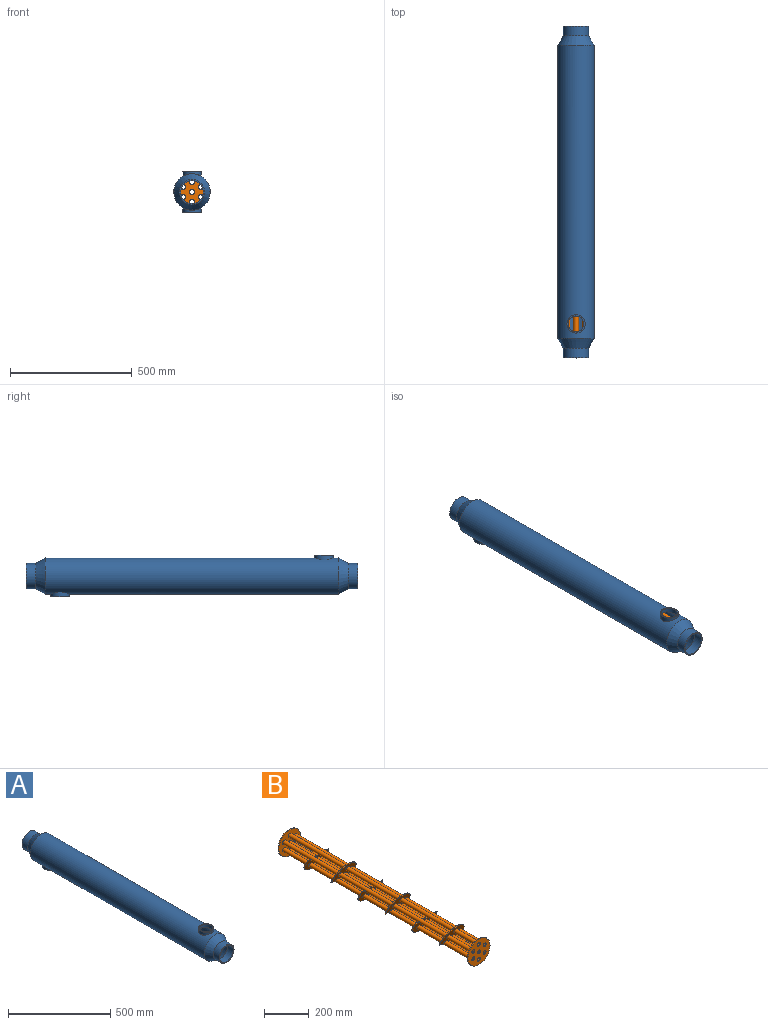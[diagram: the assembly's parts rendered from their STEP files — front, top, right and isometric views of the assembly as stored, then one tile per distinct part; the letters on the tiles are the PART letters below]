
ASSEMBLY  parts=2 mates=2
PART A: 18 faces, bbox 150x1365x170 mm
  f0: cylinder r=75mm len=1205mm, axis (0,-1,0), area 558717mm2, adj f2,f3,f14,f17
  f1: cylinder r=70mm len=1205mm, axis (0,-1,0), area 523166.6mm2, adj f7,f8,f12,f15
  f2: cone r=51.8mm half-angle=30.1deg, axis (0,-1,0), area 18420.3mm2, adj f0,f11
  f3: cone r=51.8mm half-angle=30.1deg, axis (0,1,0), area 18420.3mm2, adj f0,f4
  f4: cylinder r=51.8mm len=103.6mm, axis (0,-1,0), area 13018.8mm2, adj f3,f5
  f5: plane 103.6x103.6mm, normal (0,-1,0), area 1548.8mm2, adj f4,f6
  f6: cylinder r=46.8mm len=93.6mm, axis (0,-1,0), area 11762.2mm2, adj f5,f7
  f7: cone r=70mm half-angle=30.1deg, axis (0,1,0), area 16967.6mm2, adj f1,f6
  f8: cone r=70mm half-angle=30.1deg, axis (0,-1,0), area 16967.6mm2, adj f1,f9
  f9: cylinder r=46.8mm len=93.6mm, axis (0,-1,0), area 11762.2mm2, adj f8,f10
  f10: plane 103.6x103.6mm, normal (0,1,0), area 1548.8mm2, adj f9,f11
  f11: cylinder r=51.8mm len=103.6mm, axis (0,-1,0), area 13018.8mm2, adj f2,f10
  f12: cylinder r=32.5mm len=65mm, axis (0,0,1), area 3866.5mm2, adj f1,f16
  f13: plane 75x75mm, normal (0,0,-1), area 1099.6mm2, adj f14,f15
  f14: cylinder r=37.5mm len=75mm, axis (0,0,-1), area 3518.8mm2, adj f0,f13
  f15: cylinder r=32.5mm len=65mm, axis (0,0,-1), area 3867.9mm2, adj f1,f13
  f16: plane 75x75mm, normal (0,0,1), area 1099.6mm2, adj f12,f17
  f17: cylinder r=37.5mm len=75mm, axis (0,0,1), area 3518.1mm2, adj f0,f16
PART B: 80 faces, bbox 142.1x1207.1x142.1 mm
  f0: plane 140x140mm, normal (0,1,0), area 13409.1mm2, adj f1,f3,f4,f5,f6,f7,f8,f9
  f1: cylinder r=70mm len=140mm, axis (0,1,0), area 2199.1mm2, adj f0,f2
  f2: plane 140x140mm, normal (0,-1,0), area 12969.3mm2, adj f1,f10,f12,f13,f14,f15,f16,f18
  f3: cylinder r=9.5mm len=1205mm, axis (0,-1,0), area 71926.8mm2, adj f0,f11
  f4: cylinder r=9.5mm len=1205mm, axis (0,-1,0), area 71926.8mm2, adj f0,f11
  f5: cylinder r=9.5mm len=1205mm, axis (0,-1,0), area 71926.8mm2, adj f0,f11
  f6: cylinder r=9.5mm len=1205mm, axis (0,-1,0), area 71926.8mm2, adj f0,f11
  f7: cylinder r=9.5mm len=1205mm, axis (0,-1,0), area 71926.8mm2, adj f0,f11
  f8: cylinder r=9.5mm len=1205mm, axis (0,-1,0), area 71926.8mm2, adj f0,f11
  f9: cylinder r=9.5mm len=1205mm, axis (0,-1,0), area 71926.8mm2, adj f0,f11
  f10: cylinder r=10.5mm len=352.06mm, axis (0,-1,0), area 22715.9mm2, adj f2,f50,f55,f56,f58,f59
  f11: plane 140x140mm, normal (0,-1,0), area 13409.1mm2, adj f3,f4,f5,f6,f7,f8,f9,f61
  f12: cylinder r=10.5mm len=161.51mm, axis (0,-1,0), area 10332.2mm2, adj f2,f56
  f13: cylinder r=10.5mm len=151.95mm, axis (0,-1,0), area 9701.6mm2, adj f2,f56
  f14: cylinder r=10.5mm len=161.51mm, axis (0,-1,0), area 10332.2mm2, adj f2,f56
  f15: cylinder r=10.5mm len=352.06mm, axis (0,-1,0), area 22715.9mm2, adj f2,f50,f54,f55,f56,f58
  f16: cylinder r=10.5mm len=361.62mm, axis (0,-1,0), area 23534.1mm2, adj f2,f50
  f17: cylinder r=10.5mm len=171.06mm, axis (0,-1,0), area 10962.3mm2, adj f28,f60
  f18: cylinder r=10.5mm len=171.07mm, axis (0,-1,0), area 10962.9mm2, adj f2,f56
  f19: cylinder r=10.5mm len=175.78mm, axis (0,-1,0), area 10945.9mm2, adj f50,f58
  f20: cylinder r=10.5mm len=175.78mm, axis (0,-1,0), area 10945.9mm2, adj f44,f52
  f21: cylinder r=10.5mm len=175.78mm, axis (0,-1,0), area 10945.9mm2, adj f38,f46
  f22: cylinder r=10.5mm len=175.78mm, axis (0,-1,0), area 10945.9mm2, adj f32,f40
  f23: cylinder r=10.5mm len=175.78mm, axis (0,-1,0), area 10945.9mm2, adj f26,f34
  f24: plane 50.04x5.52mm, normal (0,0,-1), area 276.1mm2, adj f26,f28,f70,f76
  f25: plane 20.78x5.52mm, normal (0,0,-1), area 114.6mm2, adj f26,f27,f28,f76
  f26: plane 140x91mm, normal (0,0.91,0.42), area 9753.2mm2, adj f23,f24,f25,f27,f29,f63,f66,f70
  f27: cylinder r=70mm len=140mm, axis (0,1,0), area 1448.6mm2, adj f25,f26,f28,f29
  f28: plane 142.06x93.06mm, normal (0,-0.91,-0.42), area 9753.2mm2, adj f17,f24,f25,f27,f29,f64,f67,f70
  f29: plane 20.78x5.52mm, normal (0,0,-1), area 114.6mm2, adj f26,f27,f28,f70
  f30: plane 20.78x5.52mm, normal (0,0,1), area 114.6mm2, adj f32,f33,f34,f66
  f31: plane 50.04x5.52mm, normal (0,0,1), area 276.1mm2, adj f32,f34,f66,f78
  f32: plane 140x91mm, normal (0,0.91,0.42), area 9753.2mm2, adj f22,f30,f31,f33,f35,f66,f69,f72
  f33: cylinder r=70mm len=140mm, axis (0,1,0), area 1448.6mm2, adj f30,f32,f34,f35
  f34: plane 142.06x93.06mm, normal (0,-0.91,-0.42), area 9753.2mm2, adj f23,f30,f31,f33,f35,f66,f70,f73
  f35: plane 20.78x5.52mm, normal (0,0,1), area 114.6mm2, adj f32,f33,f34,f78
  f36: plane 50.04x5.52mm, normal (0,0,-1), area 276.1mm2, adj f38,f40,f69,f75
  f37: plane 20.78x5.52mm, normal (0,0,-1), area 114.6mm2, adj f38,f39,f40,f75
  f38: plane 142.13x93.13mm, normal (0,0.91,0.42), area 9753.2mm2, adj f21,f36,f37,f39,f41,f62,f65,f69
  f39: cylinder r=70mm len=140mm, axis (0,1,0), area 1448.6mm2, adj f37,f38,f40,f41
  f40: plane 142.13x93.13mm, normal (0,-0.91,-0.42), area 9753.2mm2, adj f22,f36,f37,f39,f41,f63,f66,f69
  f41: plane 20.78x5.52mm, normal (0,0,-1), area 114.6mm2, adj f38,f39,f40,f69
  f42: plane 20.78x5.52mm, normal (0,0,1), area 114.6mm2, adj f44,f45,f46,f65
  f43: plane 50.04x5.52mm, normal (0,0,1), area 276.1mm2, adj f44,f46,f65,f77
  f44: plane 140x91mm, normal (0,0.91,0.42), area 9753.2mm2, adj f20,f42,f43,f45,f47,f65,f68,f71
  f45: cylinder r=70mm len=140mm, axis (0,1,0), area 1448.6mm2, adj f42,f44,f46,f47
  f46: plane 140x91mm, normal (0,-0.91,-0.42), area 9753.2mm2, adj f21,f42,f43,f45,f47,f65,f69,f72
  f47: plane 20.78x5.52mm, normal (0,0,1), area 114.6mm2, adj f44,f45,f46,f77
  f48: plane 50.04x5.52mm, normal (0,0,-1), area 276.1mm2, adj f50,f52,f68,f74
  f49: plane 20.78x5.52mm, normal (0,0,-1), area 114.6mm2, adj f50,f51,f52,f74
  f50: plane 142.13x93.13mm, normal (0,0.91,0.42), area 9753.2mm2, adj f10,f15,f16,f19,f48,f49,f51,f53
  f51: cylinder r=70mm len=140mm, axis (0,1,0), area 1448.6mm2, adj f49,f50,f52,f53
  f52: plane 142.13x93.13mm, normal (0,-0.91,-0.42), area 9753.2mm2, adj f20,f48,f49,f51,f53,f62,f65,f68
  f53: plane 20.78x5.52mm, normal (0,0,-1), area 114.6mm2, adj f50,f51,f52,f68
  f54: plane 20.78x5.52mm, normal (0,0,1), area 114.6mm2, adj f15,f56,f57,f58
  f55: plane 50.04x5.52mm, normal (0,0,1), area 276.1mm2, adj f10,f15,f56,f58
  f56: plane 142.13x93.13mm, normal (0,0.91,0.42), area 9753.2mm2, adj f10,f12,f13,f14,f15,f18,f54,f55
  f57: cylinder r=70mm len=140mm, axis (0,1,0), area 1448.6mm2, adj f54,f56,f58,f59
  f58: plane 142.13x93.13mm, normal (0,-0.91,-0.42), area 9753.2mm2, adj f10,f15,f19,f54,f55,f57,f59,f68
  f59: plane 20.78x5.52mm, normal (0,0,1), area 114.6mm2, adj f10,f56,f57,f58
  f60: plane 140x140mm, normal (0,1,0), area 12969.3mm2, adj f17,f61,f64,f67,f70,f73,f76,f79
  f61: cylinder r=70mm len=140mm, axis (0,1,0), area 2199.1mm2, adj f11,f60
  f62: cylinder r=10.5mm len=347.21mm, axis (0,-1,0), area 22255.7mm2, adj f38,f52
  f63: cylinder r=10.5mm len=347.21mm, axis (0,-1,0), area 22255.7mm2, adj f26,f40
  f64: cylinder r=10.5mm len=151.94mm, axis (0,-1,0), area 9700.9mm2, adj f28,f60
  f65: cylinder r=10.5mm len=347.21mm, axis (0,-1,0), area 22068.2mm2, adj f38,f42,f43,f44,f46,f52
  f66: cylinder r=10.5mm len=347.21mm, axis (0,-1,0), area 22068.2mm2, adj f26,f30,f31,f32,f34,f40
  f67: cylinder r=10.5mm len=161.5mm, axis (0,-1,0), area 10331.6mm2, adj f28,f60
  f68: cylinder r=10.5mm len=347.21mm, axis (0,-1,0), area 22068.2mm2, adj f44,f48,f50,f52,f53,f58
  f69: cylinder r=10.5mm len=347.21mm, axis (0,-1,0), area 22068.2mm2, adj f32,f36,f38,f40,f41,f46
  f70: cylinder r=10.5mm len=352.05mm, axis (0,-1,0), area 22715.2mm2, adj f24,f26,f28,f29,f34,f60
  f71: cylinder r=10.5mm len=347.21mm, axis (0,-1,0), area 22255.7mm2, adj f44,f58
  f72: cylinder r=10.5mm len=347.21mm, axis (0,-1,0), area 22255.7mm2, adj f32,f46
  f73: cylinder r=10.5mm len=361.61mm, axis (0,-1,0), area 23533.4mm2, adj f34,f60
  f74: cylinder r=10.5mm len=347.21mm, axis (0,-1,0), area 22068.2mm2, adj f44,f48,f49,f50,f52,f58
  f75: cylinder r=10.5mm len=347.21mm, axis (0,-1,0), area 22068.2mm2, adj f32,f36,f37,f38,f40,f46
  f76: cylinder r=10.5mm len=352.05mm, axis (0,-1,0), area 22715.2mm2, adj f24,f25,f26,f28,f34,f60
  f77: cylinder r=10.5mm len=347.21mm, axis (0,-1,0), area 22068.2mm2, adj f38,f43,f44,f46,f47,f52
  f78: cylinder r=10.5mm len=347.21mm, axis (0,-1,0), area 22068.2mm2, adj f26,f31,f32,f34,f35,f40
  f79: cylinder r=10.5mm len=161.5mm, axis (0,-1,0), area 10331.6mm2, adj f28,f60
PLACE A t=(-386.59,-470.4,-370.8)mm
PLACE B t=(-386.59,129.6,-370.8)mm
MATE cylindrical A.f0 <-> B.f1  axis (0,-1,0) through (-386.59,-470.4,-370.8)mm
MATE fastened A.f0 <-> B.f1  axis (0,-1,0) through (-386.59,-1072.9,-370.8)mm
